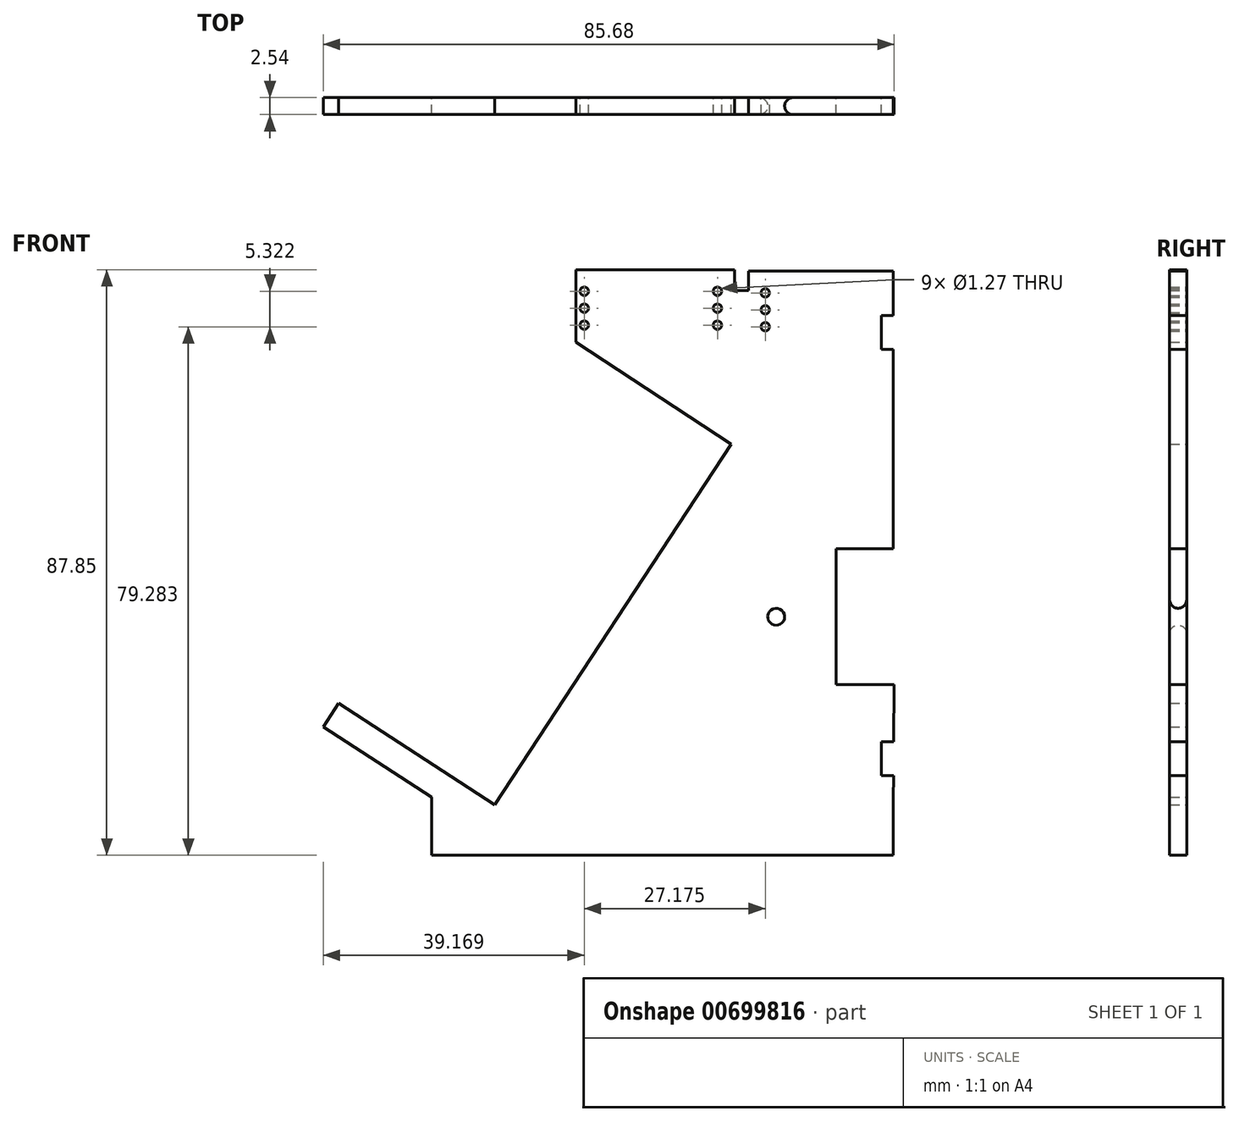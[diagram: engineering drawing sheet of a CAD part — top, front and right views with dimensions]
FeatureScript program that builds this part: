
annotation { "Feature Type Name" : "Feature", "Feature Type Description" : "" }
export const myFeature = defineFeature(function(context is Context, id is Id, definition is map)
    precondition{}
    {
        {
            var Q0;
            Q0=qCreatedBy(makeId("Front.planeOp"),FACE);
            var sketch = newSketch(context, id + "F0", { "sketchPlane" : qUnion([Q0])});
            skLineSegment(sketch, "E0.top", {"start": v(-8.7, 33.9) * mm, "end": v(15.1, 33.9) * mm});
            skLineSegment(sketch, "E0.right", {"start": v(15.1, 30.78) * mm, "end": v(15.1, 33.9) * mm});
            skLineSegment(sketch, "E1.top", {"start": v(15.1, 30.78) * mm, "end": v(17.2, 30.78) * mm});
            skLineSegment(sketch, "E1.right", {"start": v(38.95, 5.32) * mm, "end": v(38.95, 21.94) * mm});
            skPoint(sketch, "E2.orphan", {"position": v(38.95, -45.48) * mm});
            skLineSegment(sketch, "E3", {"start": v(39.35, 5) * mm, "end": v(39.24, -7.98) * mm});
            skLineSegment(sketch, "E4.top", {"start": v(39.24, -28.39) * mm, "end": v(39.08, -28.39) * mm});
            skLineSegment(sketch, "E5.trimOffspring", {"start": v(39.08, -28.39) * mm, "end": v(39.02, -36.93) * mm});
            skLineSegment(sketch, "E6.right", {"start": v(38.95, 30.78) * mm, "end": v(38.95, 27.02) * mm});
            skLineSegment(sketch, "E7.bottom", {"start": v(39.24, -7.98) * mm, "end": v(30.35, -7.98) * mm});
            skLineSegment(sketch, "E7.top", {"start": v(39.24, -28.39) * mm, "end": v(30.35, -28.39) * mm});
            skLineSegment(sketch, "E7.right", {"start": v(30.35, -7.98) * mm, "end": v(30.35, -28.39) * mm});
            skLineSegment(sketch, "E8.trimOffspring", {"start": v(38.95, -28.39) * mm, "end": v(38.95, -36.93) * mm});
            skPoint(sketch, "E9.orphan", {"position": v(-64, 19.6) * mm});
            skLineSegment(sketch, "E10.trimOffspring", {"start": v(-8.7, 23.02) * mm, "end": v(-8.7, 33.9) * mm});
            skLineSegment(sketch, "E11.trimOffspring", {"start": v(-8.7, 23.02) * mm, "end": v(-8.7, 30.64) * mm});
            skPoint(sketch, "E12.endSnap0", {"position": v(-8.7, 25.56) * mm});
            skLineSegment(sketch, "E13.trimOffspring", {"start": v(-8.7, 23.02) * mm, "end": v(-8.7, 28.59) * mm});
            skPoint(sketch, "E14.orphan", {"position": v(-8.7, 20.5) * mm});
            skLineSegment(sketch, "E15.top", {"start": v(17.2, 33.65) * mm, "end": v(38.95, 33.65) * mm});
            skLineSegment(sketch, "E15.left", {"start": v(17.2, 30.78) * mm, "end": v(17.2, 33.65) * mm});
            skLineSegment(sketch, "E15.right", {"start": v(38.95, 30.78) * mm, "end": v(38.95, 33.65) * mm});
            skPoint(sketch, "E16.end.orphan", {"position": v(-56.78, -28.13) * mm});
            skPoint(sketch, "E16.start.orphan", {"position": v(-54.5, -24.6) * mm});
            skPoint(sketch, "E17.start.orphan", {"position": v(-43.55, -36.67) * mm});
            skPoint(sketch, "E18.end.orphan", {"position": v(-41.27, -33.14) * mm});
            skPoint(sketch, "E18.start.orphan", {"position": v(-28.04, -41.7) * mm});
            skLineSegment(sketch, "E19", {"start": v(-44.32, -31.17) * mm, "end": v(-46.6, -34.7) * mm});
            skLineSegment(sketch, "E20", {"start": v(-20.88, -46.38) * mm, "end": v(14.65, 7.68) * mm});
            skLineSegment(sketch, "E21", {"start": v(-30.32, -45.22) * mm, "end": v(-30.32, -53.96) * mm});
            skLineSegment(sketch, "E22", {"start": v(38.95, -45.48) * mm, "end": v(38.95, -53.96) * mm});
            skLineSegment(sketch, "E23", {"start": v(38.95, -53.96) * mm, "end": v(-30.32, -53.96) * mm});
            skPoint(sketch, "E24.end.orphan", {"position": v(-10.8, 30.78) * mm});
            skPoint(sketch, "E24.start.orphan", {"position": v(-8.7, 30.78) * mm});
            skLineSegment(sketch, "E25.left", {"start": v(-8.7, 23.02) * mm, "end": v(-8.7, 38.26) * mm});
            skPoint(sketch, "E26.start.orphan", {"position": v(-9.4, 21.96) * mm});
            skLineSegment(sketch, "E27", {"start": v(-8.7, 23.02) * mm, "end": v(-8.7, 23.02) * mm});
            skPoint(sketch, "E28.end.orphan", {"position": v(-9.05, 23.02) * mm});
            skPoint(sketch, "E29.orphan", {"position": v(-9.4, 23.02) * mm});
            skLineSegment(sketch, "E30", {"start": v(14.65, 7.68) * mm, "end": v(-8.7, 23.02) * mm});
            skLineSegment(sketch, "E31", {"start": v(-20.88, -46.38) * mm, "end": v(-44.33, -31.19) * mm});
            skLineSegment(sketch, "E32", {"start": v(-46.6, -34.7) * mm, "end": v(-30.32, -45.22) * mm});
            skLineSegment(sketch, "E33.bottom", {"start": v(38.95, 27.02) * mm, "end": v(37.17, 27.02) * mm});
            skLineSegment(sketch, "E33.top", {"start": v(38.95, 21.94) * mm, "end": v(37.17, 21.94) * mm});
            skLineSegment(sketch, "E33.right", {"start": v(37.17, 27.02) * mm, "end": v(37.17, 21.94) * mm});
            skLineSegment(sketch, "E34.trimOffspring", {"start": v(38.95, 21.94) * mm, "end": v(38.95, -7.98) * mm});
            skLineSegment(sketch, "E35.trimOffspring", {"start": v(38.95, 27.02) * mm, "end": v(38.95, 30.78) * mm});
            skLineSegment(sketch, "E36.bottom", {"start": v(39.02, -36.93) * mm, "end": v(37.17, -36.93) * mm});
            skLineSegment(sketch, "E36.top", {"start": v(39.02, -42.01) * mm, "end": v(37.17, -42.01) * mm});
            skLineSegment(sketch, "E36.right", {"start": v(37.17, -36.93) * mm, "end": v(37.17, -42.01) * mm});
            skLineSegment(sketch, "E37.trimOffspring", {"start": v(38.95, -42.01) * mm, "end": v(38.95, -45.48) * mm});
            skLineSegment(sketch, "E38.trimOffspring", {"start": v(38.98, -42.01) * mm, "end": v(38.95, -45.48) * mm});
            skLineSegment(sketch, "E39", {"start": v(-7.43, 24.93) * mm, "end": v(-7.43, 26.2) * mm});
            skLineSegment(sketch, "E40", {"start": v(-8.07, 25.56) * mm, "end": v(-6.8, 25.56) * mm});
            skLineSegment(sketch, "E41", {"start": v(-6.8, 28.1) * mm, "end": v(-8.07, 28.1) * mm});
            skLineSegment(sketch, "E42", {"start": v(-8.7, 28.1) * mm, "end": v(-8.7, 30.64) * mm});
            skLineSegment(sketch, "E43", {"start": v(-8.07, 30.64) * mm, "end": v(-6.8, 30.64) * mm});
            skCircle(sketch, "E44", {"center": v(-7.43, 30.64) * mm, "radius": 0.64 * mm});
            skCircle(sketch, "E45", {"center": v(-7.43, 28.1) * mm, "radius": 0.64 * mm});
            skCircle(sketch, "E46", {"center": v(-7.43, 25.56) * mm, "radius": 0.64 * mm});
            skPoint(sketch, "E47.orphan", {"position": v(-7.43, 23.02) * mm});
            skPoint(sketch, "E48.orphan", {"position": v(-6.16, 23.02) * mm});
            skLineSegment(sketch, "E49.trimOffspring", {"start": v(-7.43, 27.47) * mm, "end": v(-7.43, 28.74) * mm});
            skPoint(sketch, "E50.orphan", {"position": v(-6.16, 28.1) * mm});
            skLineSegment(sketch, "E51.trimOffspring", {"start": v(-7.43, 30) * mm, "end": v(-7.43, 31.28) * mm});
            skPoint(sketch, "E52.orphan", {"position": v(-6.16, 25.56) * mm});
            skPoint(sketch, "E53.orphan", {"position": v(-6.16, 30.64) * mm});
            skLineSegment(sketch, "E54", {"start": v(-8.7, 23.02) * mm, "end": v(37.17, 23.02) * mm});
            skLineSegment(sketch, "E55", {"start": v(12.56, 24.93) * mm, "end": v(12.56, 26.2) * mm});
            skLineSegment(sketch, "E56", {"start": v(12.56, 25.56) * mm, "end": v(13.2, 25.56) * mm});
            skLineSegment(sketch, "E57", {"start": v(12.56, 28.1) * mm, "end": v(13.2, 28.1) * mm});
            skLineSegment(sketch, "E58", {"start": v(12.56, 30.64) * mm, "end": v(13.2, 30.64) * mm});
            skCircle(sketch, "E59", {"center": v(12.56, 30.64) * mm, "radius": 0.64 * mm});
            skCircle(sketch, "E60", {"center": v(12.56, 25.56) * mm, "radius": 0.64 * mm});
            skCircle(sketch, "E61", {"center": v(12.56, 28.1) * mm, "radius": 0.64 * mm});
            skLineSegment(sketch, "E62.trimOffspring", {"start": v(12.56, 27.47) * mm, "end": v(12.56, 31.28) * mm});
            skCircle(sketch, "E63.MirrorC", {"center": v(19.74, 30.4) * mm, "radius": 0.64 * mm});
            skCircle(sketch, "E64.MirrorC", {"center": v(19.74, 27.86) * mm, "radius": 0.64 * mm});
            skCircle(sketch, "E65.MirrorC", {"center": v(19.74, 25.32) * mm, "radius": 0.64 * mm});
            skPoint(sketch, "E66.start.orphan", {"position": v(16.15, 30.78) * mm});
            skLineSegment(sketch, "E67", {"start": v(15.1, 33.9) * mm, "end": v(33.91, 33.9) * mm});
            skLineSegment(sketch, "E68", {"start": v(4.31, -53.96) * mm, "end": v(4.31, -8.05) * mm});
            skLineSegment(sketch, "E69", {"start": v(4.31, -8.05) * mm, "end": v(4.31, -53.96) * mm});
            skLineSegment(sketch, "E70", {"start": v(21.38, -53.96) * mm, "end": v(21.38, 23.02) * mm});
            skLineSegment(sketch, "E71", {"start": v(30.35, -18.18) * mm, "end": v(21.38, -18.18) * mm});
            skCircle(sketch, "E72", {"center": v(21.38, -18.18) * mm, "radius": 1.27 * mm});
            skSolve(sketch);
        }
        {
            var Q0;
            Q0=qSketchRegion(id+"F0",true);
            extrude(context, id + "F1", {"entities" : qUnion([Q0]), "depth" : 2.54 * mm});
        }
        {
            var Q0;
            Q0=makeQuery(id+"F1.opExtrude","CAP_EDGE",EDGE,{"disambiguationData":[OSD([sQuery(id+"F0.wireOp",EDGE,"E72")])],"isStart":false});
            var Q1;
            Q1=makeQuery(id+"F1.opExtrude","CAP_EDGE",EDGE,{"disambiguationData":[OSD([sQuery(id+"F0.wireOp",EDGE,"E72")])],"isStart":true});
            fillet(context, id + "F2", {"entities" : qUnion([Q0, Q1]), "radius" : 1.27 * mm, "tangentPropagation" : true, "allowEdgeOverflow" : false});
        }
    });
